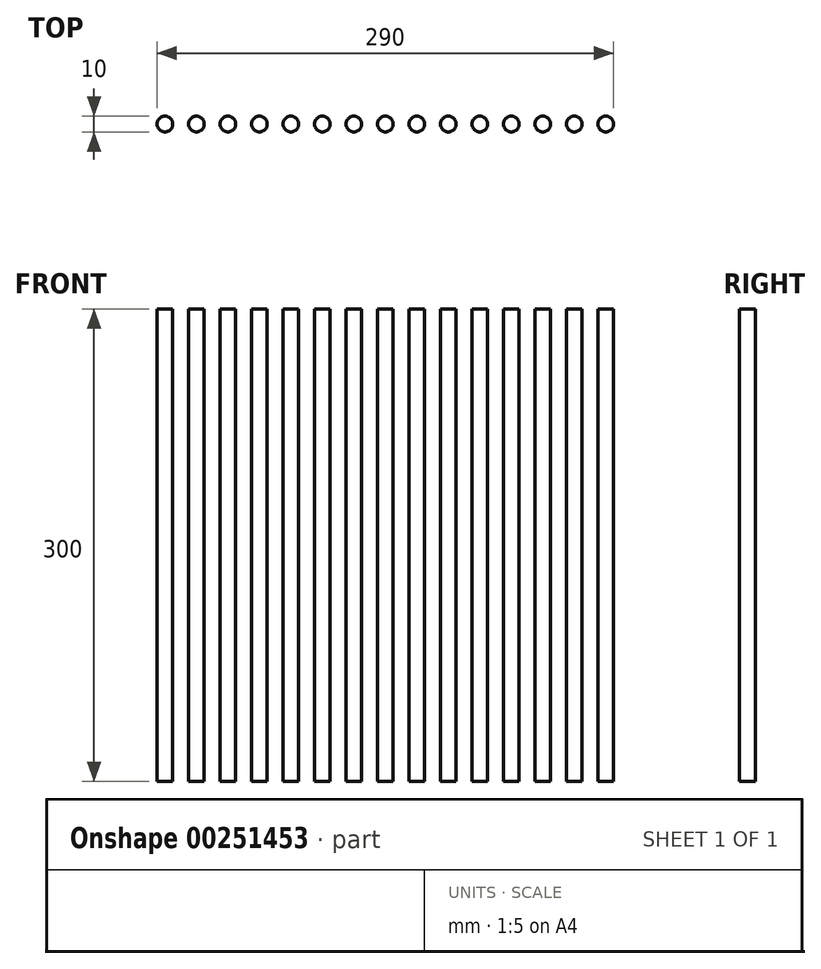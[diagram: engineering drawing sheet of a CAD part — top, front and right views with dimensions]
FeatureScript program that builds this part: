
annotation { "Feature Type Name" : "Feature", "Feature Type Description" : "" }
export const myFeature = defineFeature(function(context is Context, id is Id, definition is map)
    precondition{}
    {
        {
            var Q0;
            Q0=qCreatedBy(makeId("Top.planeOp"),FACE);
            var sketch = newSketch(context, id + "F0", { "sketchPlane" : qUnion([Q0])});
            skCircle(sketch, "E0", {"center": v(-34.02, 13.34) * mm, "radius": 5 * mm});
            skCircle(sketch, "E1", {"center": v(-14.02, 13.34) * mm, "radius": 5 * mm});
            skCircle(sketch, "E2", {"center": v(5.98, 13.34) * mm, "radius": 5 * mm});
            skCircle(sketch, "E3", {"center": v(25.98, 13.34) * mm, "radius": 5 * mm});
            skCircle(sketch, "E4", {"center": v(45.98, 13.34) * mm, "radius": 5 * mm});
            skCircle(sketch, "E5", {"center": v(65.98, 13.34) * mm, "radius": 5 * mm});
            skCircle(sketch, "E6", {"center": v(85.98, 13.34) * mm, "radius": 5 * mm});
            skCircle(sketch, "E7", {"center": v(105.98, 13.34) * mm, "radius": 5 * mm});
            skCircle(sketch, "E8", {"center": v(125.98, 13.34) * mm, "radius": 5 * mm});
            skCircle(sketch, "E9", {"center": v(145.98, 13.34) * mm, "radius": 5 * mm});
            skCircle(sketch, "E10", {"center": v(165.98, 13.34) * mm, "radius": 5 * mm});
            skCircle(sketch, "E11", {"center": v(185.98, 13.34) * mm, "radius": 5 * mm});
            skCircle(sketch, "E12", {"center": v(-94.02, 13.34) * mm, "radius": 5 * mm});
            skCircle(sketch, "E13", {"center": v(-74.02, 13.34) * mm, "radius": 5 * mm});
            skCircle(sketch, "E14", {"center": v(-54.02, 13.34) * mm, "radius": 5 * mm});
            skSolve(sketch);
        }
        {
            var Q0;
            Q0=makeQuery(id+"F0.imprint","IMPRINT",FACE,{"disambiguationData":[TD([[makeQuery(id+"F0.imprint","IMPRINT",EDGE,{"derivedFrom":sQuery(id+"F0.wireOp",EDGE,"E12")}),1.0]])]});
            var Q1;
            Q1=makeQuery(id+"F0.imprint","IMPRINT",FACE,{"disambiguationData":[TD([[makeQuery(id+"F0.imprint","IMPRINT",EDGE,{"derivedFrom":sQuery(id+"F0.wireOp",EDGE,"E13")}),1.0]])]});
            var Q2;
            Q2=makeQuery(id+"F0.imprint","IMPRINT",FACE,{"disambiguationData":[TD([[makeQuery(id+"F0.imprint","IMPRINT",EDGE,{"derivedFrom":sQuery(id+"F0.wireOp",EDGE,"E14")}),1.0]])]});
            var Q3;
            Q3=makeQuery(id+"F0.imprint","IMPRINT",FACE,{"disambiguationData":[TD([[makeQuery(id+"F0.imprint","IMPRINT",EDGE,{"derivedFrom":sQuery(id+"F0.wireOp",EDGE,"E0")}),1.0]])]});
            var Q4;
            Q4=makeQuery(id+"F0.imprint","IMPRINT",FACE,{"disambiguationData":[TD([[makeQuery(id+"F0.imprint","IMPRINT",EDGE,{"derivedFrom":sQuery(id+"F0.wireOp",EDGE,"E1")}),1.0]])]});
            var Q5;
            Q5=makeQuery(id+"F0.imprint","IMPRINT",FACE,{"disambiguationData":[TD([[makeQuery(id+"F0.imprint","IMPRINT",EDGE,{"derivedFrom":sQuery(id+"F0.wireOp",EDGE,"E2")}),1.0]])]});
            var Q6;
            Q6=makeQuery(id+"F0.imprint","IMPRINT",FACE,{"disambiguationData":[TD([[makeQuery(id+"F0.imprint","IMPRINT",EDGE,{"derivedFrom":sQuery(id+"F0.wireOp",EDGE,"E3")}),1.0]])]});
            var Q7;
            Q7=makeQuery(id+"F0.imprint","IMPRINT",FACE,{"disambiguationData":[TD([[makeQuery(id+"F0.imprint","IMPRINT",EDGE,{"derivedFrom":sQuery(id+"F0.wireOp",EDGE,"E4")}),1.0]])]});
            var Q8;
            Q8=makeQuery(id+"F0.imprint","IMPRINT",FACE,{"disambiguationData":[TD([[makeQuery(id+"F0.imprint","IMPRINT",EDGE,{"derivedFrom":sQuery(id+"F0.wireOp",EDGE,"E5")}),1.0]])]});
            var Q9;
            Q9=makeQuery(id+"F0.imprint","IMPRINT",FACE,{"disambiguationData":[TD([[makeQuery(id+"F0.imprint","IMPRINT",EDGE,{"derivedFrom":sQuery(id+"F0.wireOp",EDGE,"E6")}),1.0]])]});
            var Q10;
            Q10=makeQuery(id+"F0.imprint","IMPRINT",FACE,{"disambiguationData":[TD([[makeQuery(id+"F0.imprint","IMPRINT",EDGE,{"derivedFrom":sQuery(id+"F0.wireOp",EDGE,"E7")}),1.0]])]});
            var Q11;
            Q11=makeQuery(id+"F0.imprint","IMPRINT",FACE,{"disambiguationData":[TD([[makeQuery(id+"F0.imprint","IMPRINT",EDGE,{"derivedFrom":sQuery(id+"F0.wireOp",EDGE,"E8")}),1.0]])]});
            var Q12;
            Q12=makeQuery(id+"F0.imprint","IMPRINT",FACE,{"disambiguationData":[TD([[makeQuery(id+"F0.imprint","IMPRINT",EDGE,{"derivedFrom":sQuery(id+"F0.wireOp",EDGE,"E9")}),1.0]])]});
            var Q13;
            Q13=makeQuery(id+"F0.imprint","IMPRINT",FACE,{"disambiguationData":[TD([[makeQuery(id+"F0.imprint","IMPRINT",EDGE,{"derivedFrom":sQuery(id+"F0.wireOp",EDGE,"E10")}),1.0]])]});
            var Q14;
            Q14=makeQuery(id+"F0.imprint","IMPRINT",FACE,{"disambiguationData":[TD([[makeQuery(id+"F0.imprint","IMPRINT",EDGE,{"derivedFrom":sQuery(id+"F0.wireOp",EDGE,"E11")}),1.0]])]});
            extrude(context, id + "F1", {"entities" : qUnion([Q0, Q1, Q2, Q3, Q4, Q5, Q6, Q7, Q8, Q9, Q10, Q11, Q12, Q13, Q14]), "depth" : 300 * mm});
        }
    });
